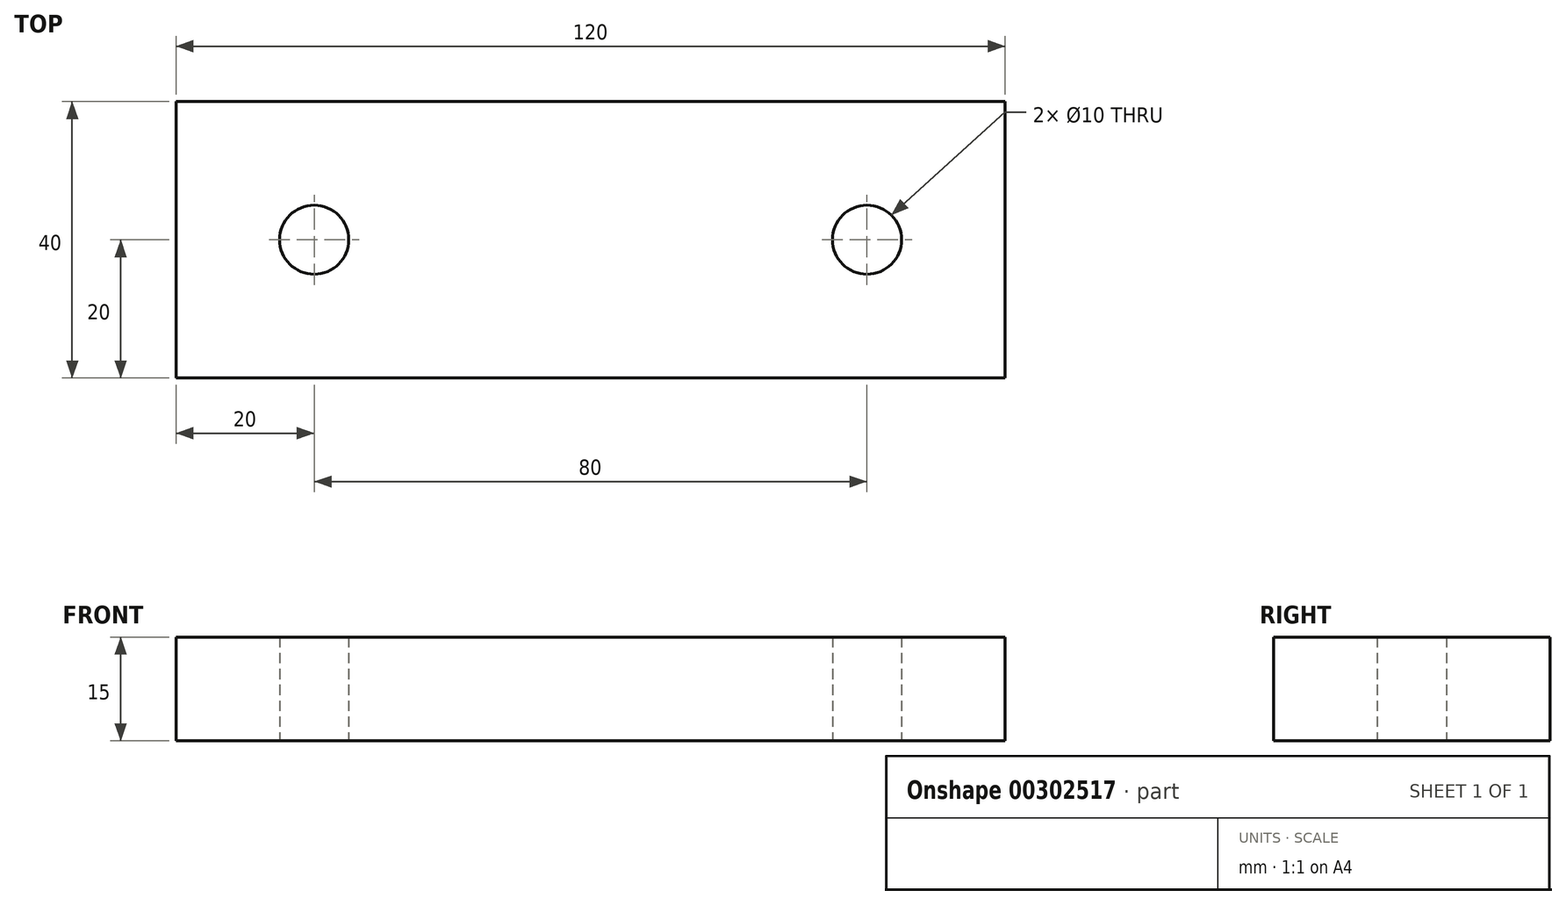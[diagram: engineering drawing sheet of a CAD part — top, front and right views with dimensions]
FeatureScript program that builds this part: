
annotation { "Feature Type Name" : "Feature", "Feature Type Description" : "" }
export const myFeature = defineFeature(function(context is Context, id is Id, definition is map)
    precondition{}
    {
        {
            var Q0;
            Q0=qCreatedBy(makeId("Top.planeOp"),FACE);
            var sketch = newSketch(context, id + "F0", { "sketchPlane" : qUnion([Q0])});
            skLineSegment(sketch, "E0.bottom", {"start": v(0, 0) * mm, "end": v(120, 0) * mm});
            skLineSegment(sketch, "E0.top", {"start": v(0, 40) * mm, "end": v(120, 40) * mm});
            skLineSegment(sketch, "E0.left", {"start": v(0, 0) * mm, "end": v(0, 40) * mm});
            skLineSegment(sketch, "E0.right", {"start": v(120, 0) * mm, "end": v(120, 40) * mm});
            skCircle(sketch, "E1", {"center": v(20, 20) * mm, "radius": 5 * mm});
            skPoint(sketch, "E1.centerSnap0", {"position": v(0, 20) * mm});
            skCircle(sketch, "E2", {"center": v(100, 20) * mm, "radius": 5 * mm});
            skPoint(sketch, "E2.centerSnap0", {"position": v(120, 20) * mm});
            skSolve(sketch);
        }
        {
            var Q0;
            Q0 = qSketchRegion(id + "F0", true);
            extrude(context, id + "F1", {"entities" : qUnion([Q0]), "depth" : 15 * mm});
        }
    });
